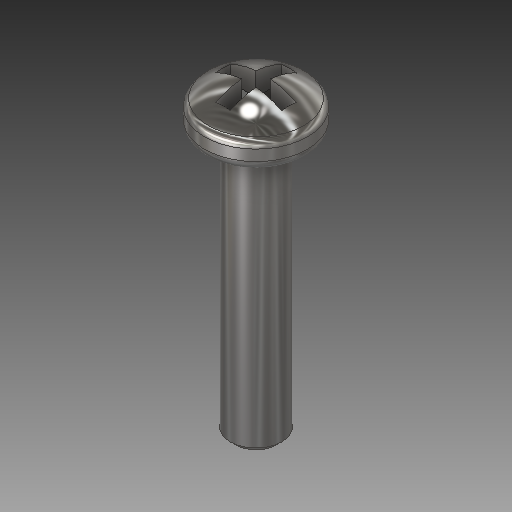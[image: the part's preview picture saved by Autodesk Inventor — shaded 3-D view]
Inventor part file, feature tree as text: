
AUTODESK INVENTOR PART (.ipt)
format: ipt  version: 2019.3 (Build 233278000, 278)  size: 244,736 bytes
history: native  units: mm
features: chamfer x2, sketch x2, revolve x1, fillet x1, plane x1, extrude x1, other x1
ambient origin geometry x8: Origin, YZ Plane, XZ Plane, XY Plane, X Axis, Y Axis, Z Axis, Center Point
bodies: Solid1 (feature_tree)
feature tree (9):
  revolve  "Revolution1"  [1 undecoded]
  chamfer  "Chamfer1"  Distance=2.5mm
  fillet  "Fillet1"  Radius=2.5mm
  plane  "Work Plane1"
  extrude  "Extrusion1"  Depth=2.5mm
  chamfer  "Chamfer2"  Angle=90.0deg  [1 undecoded]
  sketch  "Sketch1"  dims[d0=25.4mm d1=2.5mm]
  other  "Image1"
  sketch  "Sketch4"  dims[d2=4.5mm d4=2.5mm d31=2.5mm d33=2.5mm d34=90.0deg d35=0.5mm d36=2.0mm d37=45.0deg d38=1.0mm d41=0.0mm d57=2.5mm d58=1.4mm d59=2.5mm d60=1.4mm d61=2.5mm d62=2.5mm d63=1.4mm d64=90.0deg d65=2.5mm d66=1.4mm d67=90.0deg d68=3.0mm d69=0.0mm d70=0.69999mm d71=2.0mm d72=45.0deg]
note: 2 required parameter values undecoded (feature->parameter linkage not recoverable at this tier; creation-order binding heuristic only, values carry confidence <= 0.55)